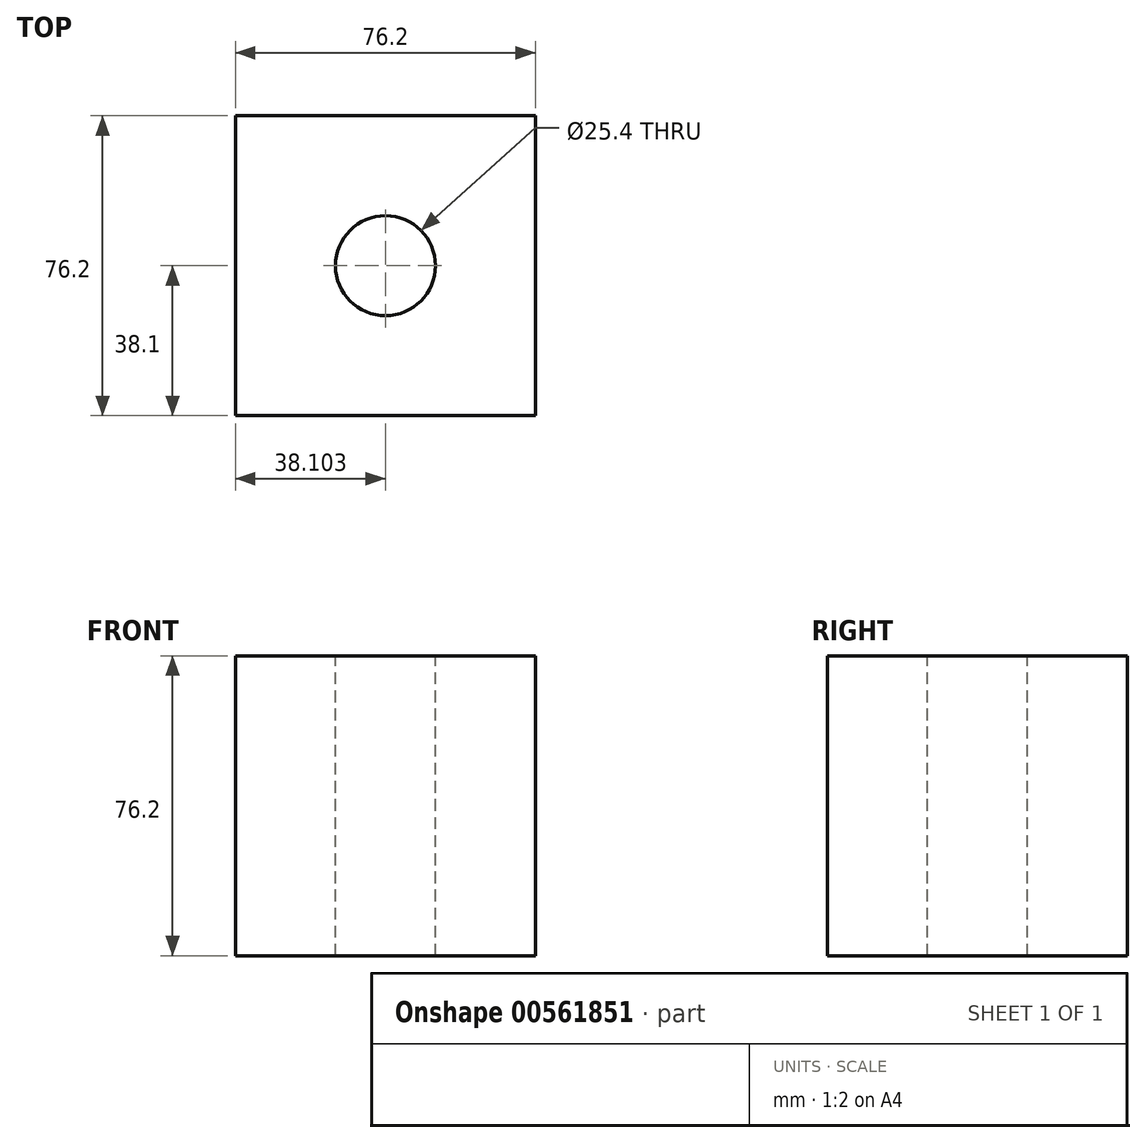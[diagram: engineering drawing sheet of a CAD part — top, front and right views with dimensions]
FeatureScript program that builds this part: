
annotation { "Feature Type Name" : "Feature", "Feature Type Description" : "" }
export const myFeature = defineFeature(function(context is Context, id is Id, definition is map)
    precondition{}
    {
        {
            var Q0;
            Q0=qCreatedBy(makeId("Front.planeOp"),FACE);
            var sketch = newSketch(context, id + "F0", { "sketchPlane" : qUnion([Q0])});
            skLineSegment(sketch, "E0.bottom", {"start": v(-37.25, -38.06) * mm, "end": v(38.95, -38.06) * mm});
            skLineSegment(sketch, "E0.top", {"start": v(-37.25, 38.14) * mm, "end": v(38.95, 38.14) * mm});
            skLineSegment(sketch, "E0.left", {"start": v(-37.25, -38.06) * mm, "end": v(-37.25, 38.14) * mm});
            skLineSegment(sketch, "E0.right", {"start": v(38.95, -38.06) * mm, "end": v(38.95, 38.14) * mm});
            skSolve(sketch);
        }
        {
            var Q0;
            Q0=makeQuery(id+"F0.imprint","IMPRINT",FACE,{"disambiguationData":[TD([[makeQuery(id+"F0.imprint","IMPRINT",EDGE,{"derivedFrom":sQuery(id+"F0.wireOp",EDGE,"E0.bottom")}),1.0]])]});
            extrude(context, id + "F1", {"entities" : qUnion([Q0]), "oppositeDirection" : true, "depth" : 76.2 * mm, "offsetDistance" : 25.4 * mm});
        }
        {
            var Q0;
            Q0=makeQuery(id+"F1.opExtrude","SWEPT_FACE",FACE,{"disambiguationData":[OSD([sQuery(id+"F0.wireOp",EDGE,"E0.top")])]});
            var sketch = newSketch(context, id + "F2", { "sketchPlane" : qUnion([Q0])});
            skPoint(sketch, "E1", {"position": v(0.85, 38.1) * mm});
            skPoint(sketch, "E1.positionSnap0", {"position": v(0.85, 0) * mm});
            skSolve(sketch);
        }
        {
            var Q0;
            Q0=sQuery(id+"F2.wireOp",VERTEX,"E1");
            var Q1;
            Q1=makeQuery(id+"F1.opExtrude","SWEPT_BODY",BODY,{"disambiguationData":[OSD([sQuery(id+"F0.wireOp",EDGE,"E0.bottom"),sQuery(id+"F0.wireOp",EDGE,"E0.top"),sQuery(id+"F0.wireOp",EDGE,"E0.left"),sQuery(id+"F0.wireOp",EDGE,"E0.right")])]});
            hole(context, id + "F3", {"style" : HoleStyle.SIMPLE, "endStyle" : HoleEndStyle.THROUGH, "holeDiameter" : 25.4 * mm, "isTappedThrough" : true, "tappedDepth" : 12.7 * mm, "tapClearance" : 3, "locations" : qUnion([Q0]), "scope" : qUnion([Q1])});
        }
    });
